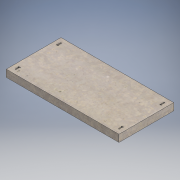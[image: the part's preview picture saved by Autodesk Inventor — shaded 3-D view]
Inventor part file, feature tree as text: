
AUTODESK INVENTOR PART (.ipt)
format: ipt  version: 2022.2 (Build 262287010, 287A)  size: 266,240 bytes
history: native  units: in
note: dims shown in document units (in); Inventor stores cm internally (conversion verified against a paired STEP export)
features: other x15, revolve x6, sketch x4, extrude x1, projected_geometry x1
ambient origin geometry x8: Origin, YZ Plane, XZ Plane, XY Plane, X Axis, Y Axis, Z Axis, Center Point
bodies: Solid1 (feature_tree)
feature tree (27):
  other  "A soffit"
  other  "Blocks"
  extrude  "Extrusion1"  Depth=23.0in
  sketch  "Sketch2"  dims[d2=47.375in d3=0.0in d4=2.0in]
  revolve  "Revolution1"  [1 undecoded]
  revolve  "Revolution2"  Angle=90.0deg
  sketch  "Sketch3"  dims[d5=1.0in d6=90.0deg]
  revolve  "Revolution3"  Angle=90.0deg
  revolve  "Revolution4"  Angle=90.0deg
  sketch  "Sketch4"  dims[d7=90.0deg d8=90.0deg d9=90.0deg d10=90.0deg d11=90.0deg]
  revolve  "Revolution5"  Angle=90.0deg
  revolve  "Revolution6"  Angle=90.0deg
  sketch  "Sketch1"  dims[d0=2.0in d1=23.0in]
  projected_geometry  "Projected Loop1"
  other  "Bolt"
  other  "Block2"
  other  "Block3"
  other  "Block2:1"
  other  "Bolt:2"
  other  "Block2:2"
  other  "Block2:4"
  other  "Block3:1"
  other  "Block3:2"
  other  "Block3:3"
  other  "Block3:4"
  other  "Block3:5"
  other  "Block3:6"
note: 1 required parameter value undecoded (feature->parameter linkage not recoverable at this tier; creation-order binding heuristic only, values carry confidence <= 0.55)
